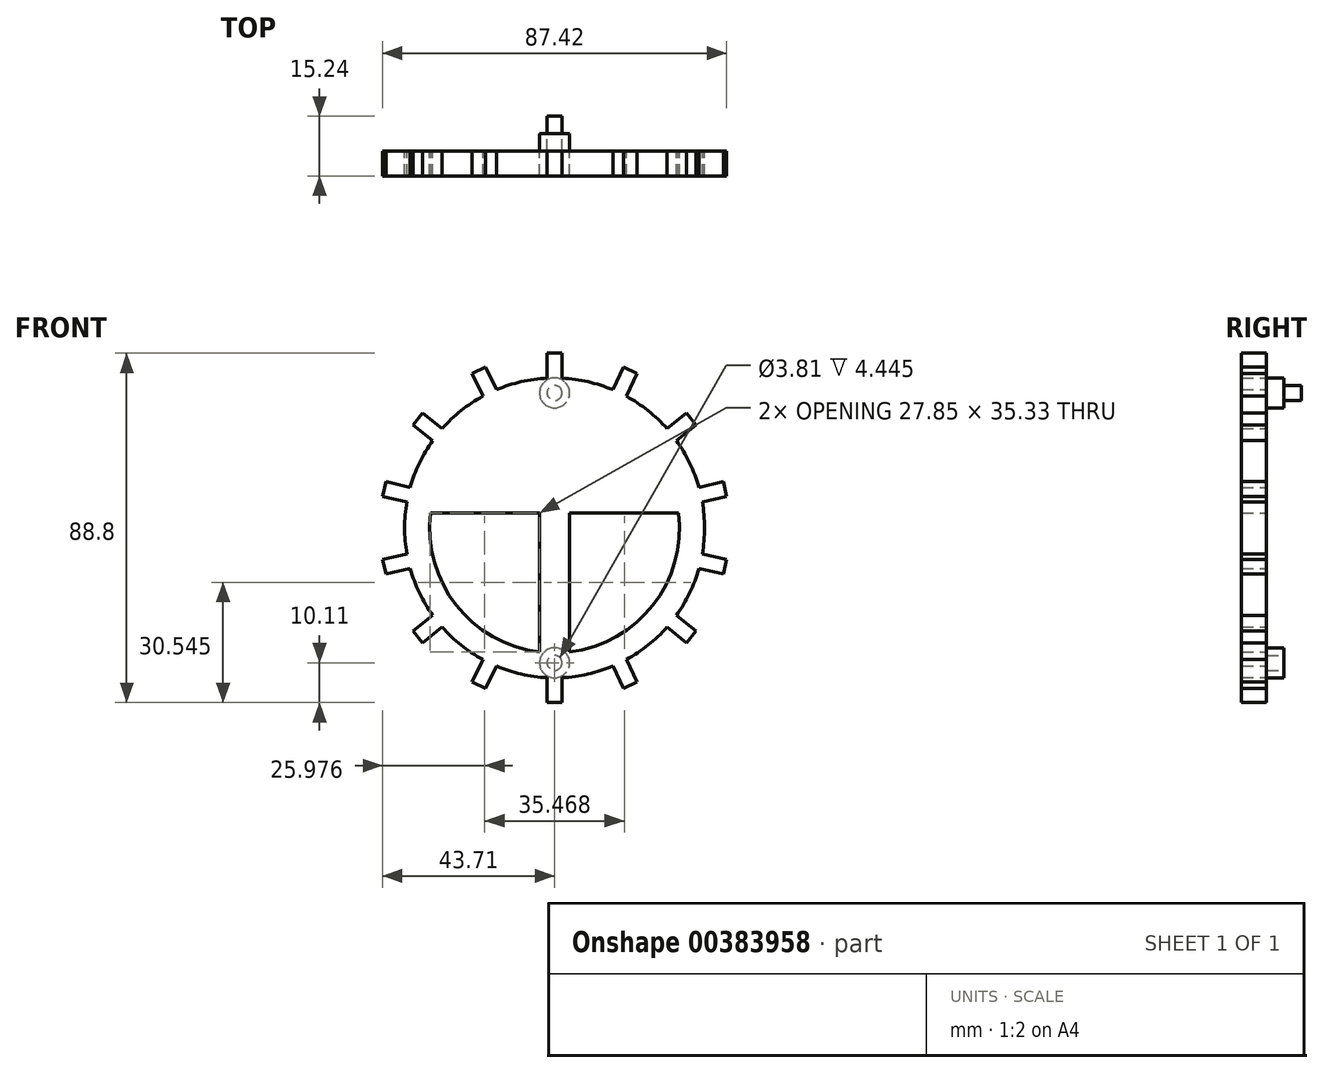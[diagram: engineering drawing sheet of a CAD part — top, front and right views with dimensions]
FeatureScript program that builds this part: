
annotation { "Feature Type Name" : "Feature", "Feature Type Description" : "" }
export const myFeature = defineFeature(function(context is Context, id is Id, definition is map)
    precondition{}
    {
        {
            var Q0;
            Q0=qCreatedBy(makeId("Front.planeOp"),FACE);
            var sketch = newSketch(context, id + "F0", { "sketchPlane" : qUnion([Q0])});
            skCircle(sketch, "E0", {"center": v(0, 0) * mm, "radius": 38.1 * mm});
            skCircle(sketch, "E1", {"center": v(0, 0) * mm, "radius": 31.75 * mm});
            skLineSegment(sketch, "E2", {"start": v(-3.81, 31.52) * mm, "end": v(-3.8, -31.52) * mm});
            skLineSegment(sketch, "E3", {"start": v(3.8, 31.52) * mm, "end": v(3.81, -31.52) * mm});
            skLineSegment(sketch, "E4", {"start": v(-31.52, 3.81) * mm, "end": v(31.52, 3.81) * mm});
            skLineSegment(sketch, "E5", {"start": v(-31.52, -3.8) * mm, "end": v(31.52, -3.8) * mm});
            skLineSegment(sketch, "E6", {"start": v(-1.9, 38.05) * mm, "end": v(-1.9, 44.4) * mm});
            skLineSegment(sketch, "E7", {"start": v(-1.9, 44.4) * mm, "end": v(1.9, 44.4) * mm});
            skLineSegment(sketch, "E8", {"start": v(1.9, 44.4) * mm, "end": v(1.9, 38.05) * mm});
            skLineSegment(sketch, "E9.1.0", {"start": v(17.55, 40.83) * mm, "end": v(20.98, 39.18) * mm});
            skLineSegment(sketch, "E9.1.1", {"start": v(20.98, 39.18) * mm, "end": v(18.23, 33.46) * mm});
            skLineSegment(sketch, "E9.1.2", {"start": v(14.8, 35.11) * mm, "end": v(17.55, 40.83) * mm});
            skLineSegment(sketch, "E9.2.0", {"start": v(33.53, 29.17) * mm, "end": v(35.9, 26.2) * mm});
            skLineSegment(sketch, "E9.2.1", {"start": v(35.9, 26.2) * mm, "end": v(30.94, 22.24) * mm});
            skLineSegment(sketch, "E9.2.2", {"start": v(28.56, 25.21) * mm, "end": v(33.53, 29.17) * mm});
            skLineSegment(sketch, "E9.3.0", {"start": v(42.87, 11.74) * mm, "end": v(43.71, 8.02) * mm});
            skLineSegment(sketch, "E9.3.1", {"start": v(43.71, 8.02) * mm, "end": v(37.52, 6.61) * mm});
            skLineSegment(sketch, "E9.3.2", {"start": v(36.67, 10.32) * mm, "end": v(42.87, 11.74) * mm});
            skLineSegment(sketch, "E9.4.0", {"start": v(43.71, -8.02) * mm, "end": v(42.87, -11.74) * mm});
            skLineSegment(sketch, "E9.4.1", {"start": v(42.87, -11.74) * mm, "end": v(36.67, -10.32) * mm});
            skLineSegment(sketch, "E9.4.2", {"start": v(37.52, -6.61) * mm, "end": v(43.71, -8.02) * mm});
            skLineSegment(sketch, "E9.5.0", {"start": v(35.9, -26.2) * mm, "end": v(33.53, -29.17) * mm});
            skLineSegment(sketch, "E9.5.1", {"start": v(33.53, -29.17) * mm, "end": v(28.56, -25.21) * mm});
            skLineSegment(sketch, "E9.5.2", {"start": v(30.94, -22.24) * mm, "end": v(35.9, -26.2) * mm});
            skLineSegment(sketch, "E9.6.0", {"start": v(20.98, -39.18) * mm, "end": v(17.55, -40.83) * mm});
            skLineSegment(sketch, "E9.6.1", {"start": v(17.55, -40.83) * mm, "end": v(14.8, -35.11) * mm});
            skLineSegment(sketch, "E9.6.2", {"start": v(18.23, -33.46) * mm, "end": v(20.98, -39.18) * mm});
            skLineSegment(sketch, "E9.7.0", {"start": v(1.9, -44.4) * mm, "end": v(-1.9, -44.4) * mm});
            skLineSegment(sketch, "E9.7.1", {"start": v(-1.9, -44.4) * mm, "end": v(-1.9, -38.05) * mm});
            skLineSegment(sketch, "E9.7.2", {"start": v(1.9, -38.05) * mm, "end": v(1.9, -44.4) * mm});
            skLineSegment(sketch, "E9.8.0", {"start": v(-17.55, -40.83) * mm, "end": v(-20.98, -39.18) * mm});
            skLineSegment(sketch, "E9.8.1", {"start": v(-20.98, -39.18) * mm, "end": v(-18.23, -33.46) * mm});
            skLineSegment(sketch, "E9.8.2", {"start": v(-14.8, -35.11) * mm, "end": v(-17.55, -40.83) * mm});
            skLineSegment(sketch, "E9.9.0", {"start": v(-33.53, -29.17) * mm, "end": v(-35.9, -26.2) * mm});
            skLineSegment(sketch, "E9.9.1", {"start": v(-35.9, -26.2) * mm, "end": v(-30.94, -22.24) * mm});
            skLineSegment(sketch, "E9.9.2", {"start": v(-28.56, -25.21) * mm, "end": v(-33.53, -29.17) * mm});
            skLineSegment(sketch, "E9.10.0", {"start": v(-42.87, -11.74) * mm, "end": v(-43.71, -8.02) * mm});
            skLineSegment(sketch, "E9.10.1", {"start": v(-43.71, -8.02) * mm, "end": v(-37.52, -6.61) * mm});
            skLineSegment(sketch, "E9.10.2", {"start": v(-36.67, -10.32) * mm, "end": v(-42.87, -11.74) * mm});
            skLineSegment(sketch, "E9.11.0", {"start": v(-43.71, 8.02) * mm, "end": v(-42.87, 11.74) * mm});
            skLineSegment(sketch, "E9.11.1", {"start": v(-42.87, 11.74) * mm, "end": v(-36.67, 10.32) * mm});
            skLineSegment(sketch, "E9.11.2", {"start": v(-37.52, 6.61) * mm, "end": v(-43.71, 8.02) * mm});
            skLineSegment(sketch, "E9.12.0", {"start": v(-35.9, 26.2) * mm, "end": v(-33.53, 29.17) * mm});
            skLineSegment(sketch, "E9.12.1", {"start": v(-33.53, 29.17) * mm, "end": v(-28.56, 25.21) * mm});
            skLineSegment(sketch, "E9.12.2", {"start": v(-30.94, 22.24) * mm, "end": v(-35.9, 26.2) * mm});
            skLineSegment(sketch, "E9.13.0", {"start": v(-20.98, 39.18) * mm, "end": v(-17.55, 40.83) * mm});
            skLineSegment(sketch, "E9.13.1", {"start": v(-17.55, 40.83) * mm, "end": v(-14.8, 35.11) * mm});
            skLineSegment(sketch, "E9.13.2", {"start": v(-18.23, 33.46) * mm, "end": v(-20.98, 39.18) * mm});
            skLineSegment(sketch, "E9.anchor1", {"start": v(0, 0) * mm, "end": v(-1.9, 38.05) * mm, "construction": true});
            skLineSegment(sketch, "E9.anchor2", {"start": v(0, 0) * mm, "end": v(-1.9, 38.05) * mm, "construction": true});
            skSolve(sketch);
        }
        {
            var Q0;
            {var subQ0=sQuery(id+"F0.wireOp",EDGE,"E0");var subQ18=makeQuery(id+"F0.imprint","INTERSECT",VERTEX,{"derivedFrom":[subQ0,sQuery(id+"F0.wireOp",EDGE,"E9.3.1")]});Q0=makeQuery(id+"F0.imprint","IMPRINT",FACE,{"disambiguationData":[TD([[makeQuery(id+"F0.imprint","IMPRINT",EDGE,{"disambiguationData":[TD([[subQ18,-1.0]])],"derivedFrom":subQ0}),1.0]])]});}
            var Q1;
            Q1=makeQuery(id+"F0.imprint","IMPRINT",FACE,{"disambiguationData":[TD([[makeQuery(id+"F0.imprint","IMPRINT",EDGE,{"derivedFrom":sQuery(id+"F0.wireOp",EDGE,"E7")}),-1.0]])]});
            var Q2;
            Q2=makeQuery(id+"F0.imprint","IMPRINT",FACE,{"disambiguationData":[TD([[makeQuery(id+"F0.imprint","IMPRINT",EDGE,{"derivedFrom":sQuery(id+"F0.wireOp",EDGE,"E9.1.0")}),-1.0]])]});
            var Q3;
            {var subQ0=sQuery(id+"F0.wireOp",EDGE,"E2");var subQ1=sQuery(id+"F0.wireOp",EDGE,"E1");var subQ2=makeQuery(id+"F0.imprint","INTERSECT",VERTEX,{"disambiguationData":[OD(0.0)],"derivedFrom":[subQ1,subQ0]});Q3=makeQuery(id+"F0.imprint","IMPRINT",FACE,{"disambiguationData":[TD([[makeQuery(id+"F0.imprint","IMPRINT",EDGE,{"disambiguationData":[TD([[subQ2,1.0]])],"derivedFrom":subQ1}),1.0]])]});}
            var Q4;
            {var subQ0=sQuery(id+"F0.wireOp",EDGE,"E2");var subQ1=sQuery(id+"F0.wireOp",EDGE,"E1");var subQ2=makeQuery(id+"F0.imprint","INTERSECT",VERTEX,{"disambiguationData":[OD(1.0)],"derivedFrom":[subQ1,subQ0]});Q4=makeQuery(id+"F0.imprint","IMPRINT",FACE,{"disambiguationData":[TD([[makeQuery(id+"F0.imprint","IMPRINT",EDGE,{"disambiguationData":[TD([[subQ2,-1.0]])],"derivedFrom":subQ1}),1.0]])]});}
            var Q5;
            {var subQ0=sQuery(id+"F0.wireOp",EDGE,"E4");var subQ1=sQuery(id+"F0.wireOp",EDGE,"E1");var subQ2=makeQuery(id+"F0.imprint","INTERSECT",VERTEX,{"disambiguationData":[OD(1.0)],"derivedFrom":[subQ1,subQ0]});Q5=makeQuery(id+"F0.imprint","IMPRINT",FACE,{"disambiguationData":[TD([[makeQuery(id+"F0.imprint","IMPRINT",EDGE,{"disambiguationData":[TD([[subQ2,1.0]])],"derivedFrom":subQ1}),1.0]])]});}
            var Q6;
            {var subQ0=sQuery(id+"F0.wireOp",EDGE,"E4");var subQ1=sQuery(id+"F0.wireOp",EDGE,"E1");var subQ2=makeQuery(id+"F0.imprint","INTERSECT",VERTEX,{"disambiguationData":[OD(0.0)],"derivedFrom":[subQ1,subQ0]});Q6=makeQuery(id+"F0.imprint","IMPRINT",FACE,{"disambiguationData":[TD([[makeQuery(id+"F0.imprint","IMPRINT",EDGE,{"disambiguationData":[TD([[subQ2,-1.0]])],"derivedFrom":subQ1}),1.0]])]});}
            var Q7;
            {var subQ0=sQuery(id+"F0.wireOp",EDGE,"E4");var subQ1=sQuery(id+"F0.wireOp",EDGE,"E2");var subQ2=makeQuery(id+"F0.imprint","INTERSECT",VERTEX,{"derivedFrom":[subQ1,subQ0]});Q7=makeQuery(id+"F0.imprint","IMPRINT",FACE,{"disambiguationData":[TD([[makeQuery(id+"F0.imprint","IMPRINT",EDGE,{"disambiguationData":[TD([[subQ2,-1.0]])],"derivedFrom":subQ1}),1.0]])]});}
            var Q8;
            Q8=makeQuery(id+"F0.imprint","IMPRINT",FACE,{"disambiguationData":[TD([[makeQuery(id+"F0.imprint","IMPRINT",EDGE,{"derivedFrom":sQuery(id+"F0.wireOp",EDGE,"E9.2.0")}),-1.0]])]});
            var Q9;
            Q9=makeQuery(id+"F0.imprint","IMPRINT",FACE,{"disambiguationData":[TD([[makeQuery(id+"F0.imprint","IMPRINT",EDGE,{"derivedFrom":sQuery(id+"F0.wireOp",EDGE,"E9.3.0")}),-1.0]])]});
            var Q10;
            Q10=makeQuery(id+"F0.imprint","IMPRINT",FACE,{"disambiguationData":[TD([[makeQuery(id+"F0.imprint","IMPRINT",EDGE,{"derivedFrom":sQuery(id+"F0.wireOp",EDGE,"E9.4.0")}),-1.0]])]});
            var Q11;
            Q11=makeQuery(id+"F0.imprint","IMPRINT",FACE,{"disambiguationData":[TD([[makeQuery(id+"F0.imprint","IMPRINT",EDGE,{"derivedFrom":sQuery(id+"F0.wireOp",EDGE,"E9.5.0")}),-1.0]])]});
            var Q12;
            Q12=makeQuery(id+"F0.imprint","IMPRINT",FACE,{"disambiguationData":[TD([[makeQuery(id+"F0.imprint","IMPRINT",EDGE,{"derivedFrom":sQuery(id+"F0.wireOp",EDGE,"E9.6.0")}),-1.0]])]});
            var Q13;
            Q13=makeQuery(id+"F0.imprint","IMPRINT",FACE,{"disambiguationData":[TD([[makeQuery(id+"F0.imprint","IMPRINT",EDGE,{"derivedFrom":sQuery(id+"F0.wireOp",EDGE,"E9.7.0")}),-1.0]])]});
            var Q14;
            Q14=makeQuery(id+"F0.imprint","IMPRINT",FACE,{"disambiguationData":[TD([[makeQuery(id+"F0.imprint","IMPRINT",EDGE,{"derivedFrom":sQuery(id+"F0.wireOp",EDGE,"E9.8.0")}),-1.0]])]});
            var Q15;
            Q15=makeQuery(id+"F0.imprint","IMPRINT",FACE,{"disambiguationData":[TD([[makeQuery(id+"F0.imprint","IMPRINT",EDGE,{"derivedFrom":sQuery(id+"F0.wireOp",EDGE,"E9.9.0")}),-1.0]])]});
            var Q16;
            Q16=makeQuery(id+"F0.imprint","IMPRINT",FACE,{"disambiguationData":[TD([[makeQuery(id+"F0.imprint","IMPRINT",EDGE,{"derivedFrom":sQuery(id+"F0.wireOp",EDGE,"E9.10.0")}),-1.0]])]});
            var Q17;
            Q17=makeQuery(id+"F0.imprint","IMPRINT",FACE,{"disambiguationData":[TD([[makeQuery(id+"F0.imprint","IMPRINT",EDGE,{"derivedFrom":sQuery(id+"F0.wireOp",EDGE,"E9.11.0")}),-1.0]])]});
            var Q18;
            Q18=makeQuery(id+"F0.imprint","IMPRINT",FACE,{"disambiguationData":[TD([[makeQuery(id+"F0.imprint","IMPRINT",EDGE,{"derivedFrom":sQuery(id+"F0.wireOp",EDGE,"E9.12.0")}),-1.0]])]});
            var Q19;
            Q19=makeQuery(id+"F0.imprint","IMPRINT",FACE,{"disambiguationData":[TD([[makeQuery(id+"F0.imprint","IMPRINT",EDGE,{"derivedFrom":sQuery(id+"F0.wireOp",EDGE,"E9.13.0")}),-1.0]])]});
            extrude(context, id + "F1", {"entities" : qUnion([Q0, Q1, Q2, Q3, Q4, Q5, Q6, Q7, Q8, Q9, Q10, Q11, Q12, Q13, Q14, Q15, Q16, Q17, Q18, Q19]), "endBound" : BoundingType.SYMMETRIC, "depth" : 6.35 * mm});
        }
        {
            var Q0;
            Q0=makeQuery(id+"F1.opExtrude","CAP_FACE",FACE,{"disambiguationData":[OSD([sQuery(id+"F0.wireOp",EDGE,"E0"),sQuery(id+"F0.wireOp",EDGE,"E1"),sQuery(id+"F0.wireOp",EDGE,"E2"),sQuery(id+"F0.wireOp",EDGE,"E3"),sQuery(id+"F0.wireOp",EDGE,"E4"),sQuery(id+"F0.wireOp",EDGE,"E5"),sQuery(id+"F0.wireOp",EDGE,"E9.1.0"),sQuery(id+"F0.wireOp",EDGE,"E9.1.1"),sQuery(id+"F0.wireOp",EDGE,"E9.1.2"),sQuery(id+"F0.wireOp",EDGE,"E9.2.0"),sQuery(id+"F0.wireOp",EDGE,"E9.2.1"),sQuery(id+"F0.wireOp",EDGE,"E9.2.2"),sQuery(id+"F0.wireOp",EDGE,"E9.3.0"),sQuery(id+"F0.wireOp",EDGE,"E9.3.1"),sQuery(id+"F0.wireOp",EDGE,"E9.3.2"),sQuery(id+"F0.wireOp",EDGE,"E9.4.0"),sQuery(id+"F0.wireOp",EDGE,"E9.4.1"),sQuery(id+"F0.wireOp",EDGE,"E9.4.2"),sQuery(id+"F0.wireOp",EDGE,"E9.5.0"),sQuery(id+"F0.wireOp",EDGE,"E9.5.1"),sQuery(id+"F0.wireOp",EDGE,"E9.5.2"),sQuery(id+"F0.wireOp",EDGE,"E9.6.0"),sQuery(id+"F0.wireOp",EDGE,"E9.6.1"),sQuery(id+"F0.wireOp",EDGE,"E9.6.2"),sQuery(id+"F0.wireOp",EDGE,"E9.7.0"),sQuery(id+"F0.wireOp",EDGE,"E9.7.1"),sQuery(id+"F0.wireOp",EDGE,"E9.7.2"),sQuery(id+"F0.wireOp",EDGE,"E9.8.0"),sQuery(id+"F0.wireOp",EDGE,"E9.8.1"),sQuery(id+"F0.wireOp",EDGE,"E9.8.2"),sQuery(id+"F0.wireOp",EDGE,"E9.9.0"),sQuery(id+"F0.wireOp",EDGE,"E9.9.1"),sQuery(id+"F0.wireOp",EDGE,"E9.9.2"),sQuery(id+"F0.wireOp",EDGE,"E9.10.0"),sQuery(id+"F0.wireOp",EDGE,"E9.10.1"),sQuery(id+"F0.wireOp",EDGE,"E9.10.2"),sQuery(id+"F0.wireOp",EDGE,"E9.11.0"),sQuery(id+"F0.wireOp",EDGE,"E9.11.1"),sQuery(id+"F0.wireOp",EDGE,"E9.11.2"),sQuery(id+"F0.wireOp",EDGE,"E9.12.0"),sQuery(id+"F0.wireOp",EDGE,"E9.12.1"),sQuery(id+"F0.wireOp",EDGE,"E9.12.2"),sQuery(id+"F0.wireOp",EDGE,"E9.13.0"),sQuery(id+"F0.wireOp",EDGE,"E9.13.1"),sQuery(id+"F0.wireOp",EDGE,"E9.13.2"),sQuery(id+"F0.wireOp",EDGE,"E7"),sQuery(id+"F0.wireOp",EDGE,"E8"),sQuery(id+"F0.wireOp",EDGE,"E6")])],"isStart":true});
            var sketch = newSketch(context, id + "F2", { "sketchPlane" : qUnion([Q0])});
            skCircle(sketch, "E10", {"center": v(0, 34.3) * mm, "radius": 3.81 * mm});
            skCircle(sketch, "E11", {"center": v(0, -34.3) * mm, "radius": 3.81 * mm});
            skSolve(sketch);
        }
        {
            var Q0;
            Q0=makeQuery(id+"F2.imprint","IMPRINT",FACE,{"disambiguationData":[TD([[makeQuery(id+"F2.imprint","IMPRINT",EDGE,{"derivedFrom":sQuery(id+"F2.wireOp",EDGE,"E10")}),1.0]])]});
            var Q1;
            Q1=makeQuery(id+"F2.imprint","IMPRINT",FACE,{"disambiguationData":[TD([[makeQuery(id+"F2.imprint","IMPRINT",EDGE,{"derivedFrom":sQuery(id+"F2.wireOp",EDGE,"E11")}),1.0]])]});
            extrude(context, id + "F3", {"entities" : qUnion([Q0, Q1]), "operationType" : NewBodyOperationType.ADD, "depth" : 4.44 * mm});
        }
        {
            var Q0;
            Q0=makeQuery(id+"F3.opExtrude","CAP_FACE",FACE,{"disambiguationData":[OSD([sQuery(id+"F2.wireOp",EDGE,"E10")])],"isStart":false});
            var sketch = newSketch(context, id + "F4", { "sketchPlane" : qUnion([Q0])});
            skCircle(sketch, "E12", {"center": v(0, 34.3) * mm, "radius": 1.9 * mm});
            skSolve(sketch);
        }
        {
            var Q0;
            Q0=makeQuery(id+"F4.imprint","IMPRINT",FACE,{"disambiguationData":[TD([[makeQuery(id+"F4.imprint","IMPRINT",EDGE,{"derivedFrom":sQuery(id+"F4.wireOp",EDGE,"E12")}),1.0]])]});
            extrude(context, id + "F5", {"entities" : qUnion([Q0]), "operationType" : NewBodyOperationType.ADD, "depth" : 4.44 * mm});
        }
        {
            var Q0;
            Q0=makeQuery(id+"F3.opExtrude","CAP_FACE",FACE,{"disambiguationData":[OSD([sQuery(id+"F2.wireOp",EDGE,"E11")])],"isStart":false});
            var sketch = newSketch(context, id + "F6", { "sketchPlane" : qUnion([Q0])});
            skCircle(sketch, "E13", {"center": v(0, -34.3) * mm, "radius": 1.9 * mm});
            skSolve(sketch);
        }
        {
            var Q0;
            Q0=makeQuery(id+"F6.imprint","IMPRINT",FACE,{"disambiguationData":[TD([[makeQuery(id+"F6.imprint","IMPRINT",EDGE,{"derivedFrom":sQuery(id+"F6.wireOp",EDGE,"E13")}),1.0]])]});
            extrude(context, id + "F7", {"entities" : qUnion([Q0]), "operationType" : NewBodyOperationType.REMOVE, "oppositeDirection" : true, "depth" : 4.44 * mm});
        }
    });
